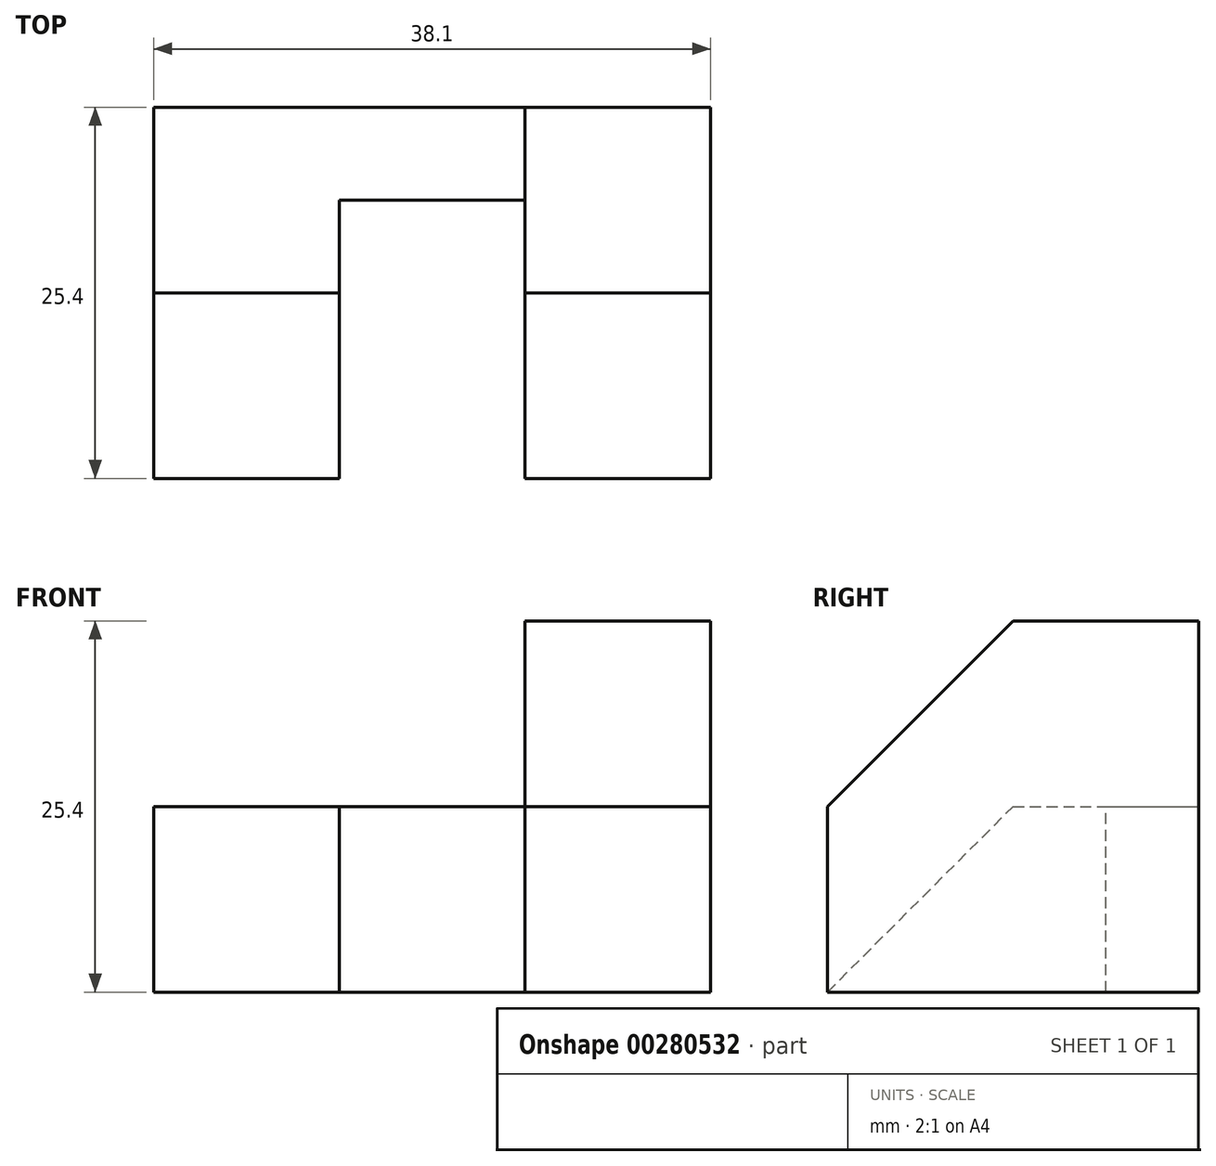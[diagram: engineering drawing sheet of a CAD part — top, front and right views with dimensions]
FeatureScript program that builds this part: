
annotation { "Feature Type Name" : "Feature", "Feature Type Description" : "" }
export const myFeature = defineFeature(function(context is Context, id is Id, definition is map)
    precondition{}
    {
        {
            var Q0;
            Q0=qCreatedBy(makeId("Right.planeOp"),FACE);
            var sketch = newSketch(context, id + "F0", { "sketchPlane" : qUnion([Q0])});
            skLineSegment(sketch, "E0", {"start": v(0, 0) * mm, "end": v(-25.4, 0) * mm});
            skLineSegment(sketch, "E1", {"start": v(-25.4, 0) * mm, "end": v(-12.7, 12.7) * mm});
            skLineSegment(sketch, "E2", {"start": v(-12.7, 12.7) * mm, "end": v(0, 12.7) * mm});
            skLineSegment(sketch, "E3", {"start": v(0, 12.7) * mm, "end": v(0, 0) * mm});
            skSolve(sketch);
        }
        {
            var Q0;
            Q0 = qSketchRegion(id + "F0", true);
            extrude(context, id + "F1", {"entities" : qUnion([Q0]), "depth" : 12.7 * mm});
        }
        {
            var Q0;
            Q0=makeQuery(id+"F1.opExtrude","CAP_FACE",FACE,{"disambiguationData":[OSD([sQuery(id+"F0.wireOp",EDGE,"E0"),sQuery(id+"F0.wireOp",EDGE,"E1"),sQuery(id+"F0.wireOp",EDGE,"E2"),sQuery(id+"F0.wireOp",EDGE,"E3")])],"isStart":false});
            var sketch = newSketch(context, id + "F2", { "sketchPlane" : qUnion([Q0])});
            skLineSegment(sketch, "E4.bottom", {"start": v(0, 0) * mm, "end": v(-6.35, 0) * mm});
            skLineSegment(sketch, "E4.top", {"start": v(0, 12.7) * mm, "end": v(-6.35, 12.7) * mm});
            skLineSegment(sketch, "E4.left", {"start": v(0, 0) * mm, "end": v(0, 12.7) * mm});
            skLineSegment(sketch, "E4.right", {"start": v(-6.35, 0) * mm, "end": v(-6.35, 12.7) * mm});
            skSolve(sketch);
        }
        {
            var Q0;
            Q0 = qSketchRegion(id + "F2", true);
            extrude(context, id + "F3", {"entities" : qUnion([Q0]), "operationType" : NewBodyOperationType.ADD, "depth" : 12.7 * mm});
        }
        {
            var Q0;
            Q0=makeQuery(id+"F3.opExtrude","CAP_FACE",FACE,{"disambiguationData":[OSD([sQuery(id+"F2.wireOp",EDGE,"E4.bottom"),sQuery(id+"F2.wireOp",EDGE,"E4.top"),sQuery(id+"F2.wireOp",EDGE,"E4.left"),sQuery(id+"F2.wireOp",EDGE,"E4.right")])],"isStart":false});
            var sketch = newSketch(context, id + "F4", { "sketchPlane" : qUnion([Q0])});
            skLineSegment(sketch, "E5", {"start": v(0, 0) * mm, "end": v(0, 25.4) * mm});
            skLineSegment(sketch, "E6", {"start": v(0, 25.4) * mm, "end": v(-12.7, 25.4) * mm});
            skLineSegment(sketch, "E7", {"start": v(-12.7, 25.4) * mm, "end": v(-25.4, 12.7) * mm});
            skLineSegment(sketch, "E8", {"start": v(-25.4, 12.7) * mm, "end": v(-25.4, 0) * mm});
            skLineSegment(sketch, "E9", {"start": v(-25.4, 0) * mm, "end": v(0, 0) * mm});
            skSolve(sketch);
        }
        {
            var Q0;
            {var subQ3=makeQuery(id+"F3.opExtrude","CAP_EDGE",EDGE,{"disambiguationData":[OSD([sQuery(id+"F2.wireOp",EDGE,"E4.top")])],"isStart":false});Q0=makeQuery(id+"F4.imprint","IMPRINT",FACE,{"disambiguationData":[TD([[makeQuery(id+"F4.imprint","IMPRINT",EDGE,{"derivedFrom":subQ3}),-1.0]])]});}
            var Q1;
            {var subQ3=sQuery(id+"F4.wireOp",EDGE,"E6");Q1=makeQuery(id+"F4.imprint","IMPRINT",FACE,{"disambiguationData":[TD([[makeQuery(id+"F4.imprint","IMPRINT",EDGE,{"derivedFrom":subQ3}),1.0]])]});}
            extrude(context, id + "F5", {"entities" : qUnion([Q0, Q1]), "operationType" : NewBodyOperationType.ADD, "depth" : 12.7 * mm});
        }
    });
